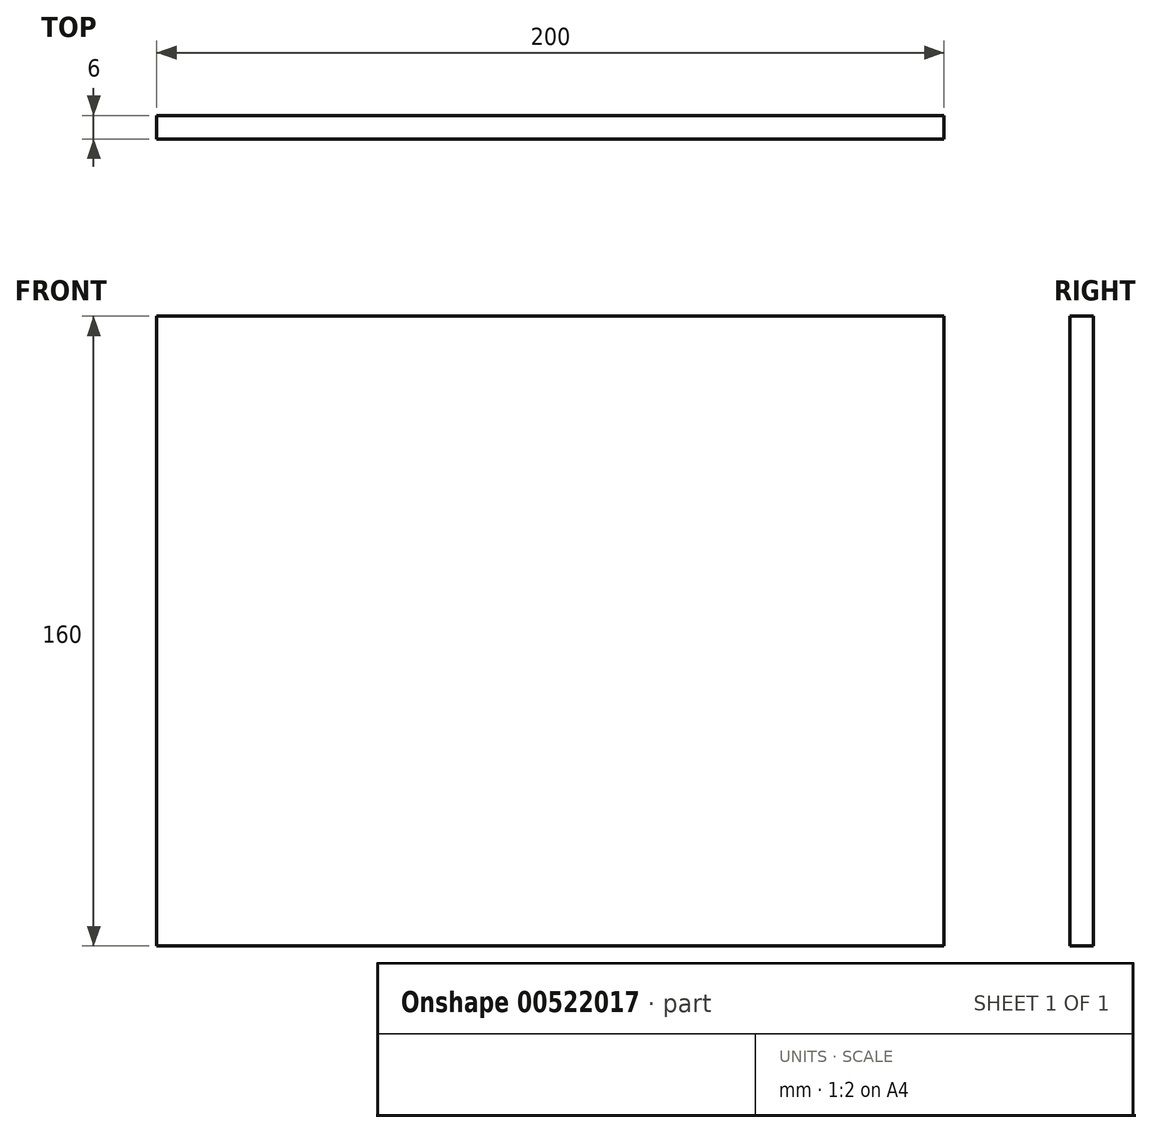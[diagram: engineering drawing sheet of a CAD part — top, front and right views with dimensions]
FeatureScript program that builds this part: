
annotation { "Feature Type Name" : "Feature", "Feature Type Description" : "" }
export const myFeature = defineFeature(function(context is Context, id is Id, definition is map)
    precondition{}
    {
        {
            var Q0;
            Q0=qCreatedBy(makeId("Front.planeOp"),FACE);
            var sketch = newSketch(context, id + "F0", { "sketchPlane" : qUnion([Q0])});
            skLineSegment(sketch, "E0.bottom", {"start": v(0, 0) * mm, "end": v(200, 0) * mm});
            skLineSegment(sketch, "E0.top", {"start": v(0, 160) * mm, "end": v(200, 160) * mm});
            skLineSegment(sketch, "E0.left", {"start": v(0, 0) * mm, "end": v(0, 160) * mm});
            skLineSegment(sketch, "E0.right", {"start": v(200, 0) * mm, "end": v(200, 160) * mm});
            skSolve(sketch);
        }
        {
            var Q0;
            Q0=makeQuery(id+"F0.imprint","IMPRINT",FACE,{"disambiguationData":[TD([[makeQuery(id+"F0.imprint","IMPRINT",EDGE,{"derivedFrom":sQuery(id+"F0.wireOp",EDGE,"E0.bottom")}),1.0]])]});
            extrude(context, id + "F1", {"entities" : qUnion([Q0]), "depth" : 6 * mm, "offsetDistance" : 25 * mm});
        }
    });
